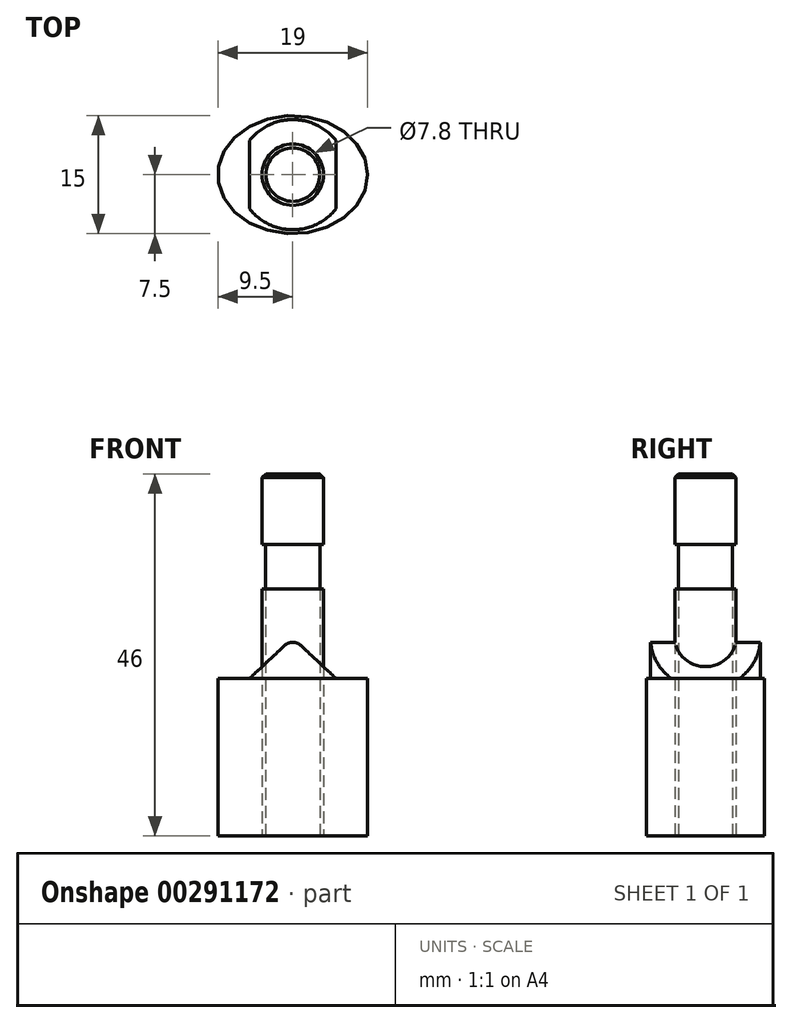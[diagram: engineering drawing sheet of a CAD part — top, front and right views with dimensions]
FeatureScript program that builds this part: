
annotation { "Feature Type Name" : "Feature", "Feature Type Description" : "" }
export const myFeature = defineFeature(function(context is Context, id is Id, definition is map)
    precondition{}
    {
        {
            var Q0;
            Q0=qCreatedBy(makeId("Top.planeOp"),FACE);
            var sketch = newSketch(context, id + "F0", { "sketchPlane" : qUnion([Q0])});
            skEllipse(sketch, "E0", {"center": v(0, 0) * mm, "majorRadius": 9.5 * mm, "minorRadius": 7.5 * mm, "majorAxis": v(1, 0)});
            skSolve(sketch);
        }
        {
            var Q0;
            Q0=makeQuery(id+"F0.imprint","IMPRINT",FACE,{"disambiguationData":[TD([[makeQuery(id+"F0.imprint","IMPRINT",EDGE,{"derivedFrom":sQuery(id+"F0.wireOp",EDGE,"E0")}),1.0]])]});
            extrude(context, id + "F1", {"entities" : qUnion([Q0]), "depth" : 20 * mm});
        }
        {
            var Q0;
            Q0=makeQuery(id+"F1.opExtrude","CAP_FACE",FACE,{"disambiguationData":[OSD([sQuery(id+"F0.wireOp",EDGE,"E0")])],"isStart":false});
            var sketch = newSketch(context, id + "F2", { "sketchPlane" : qUnion([Q0])});
            skCircle(sketch, "E1", {"center": v(0, 0) * mm, "radius": 7 * mm});
            skSolve(sketch);
        }
        {
            var Q0;
            Q0=makeQuery(id+"F2.imprint","IMPRINT",FACE,{"disambiguationData":[TD([[makeQuery(id+"F2.imprint","IMPRINT",EDGE,{"derivedFrom":sQuery(id+"F2.wireOp",EDGE,"E1")}),1.0]])]});
            extrude(context, id + "F3", {"entities" : qUnion([Q0]), "operationType" : NewBodyOperationType.ADD, "depth" : 4.6 * mm});
        }
        {
            var Q0;
            Q0=qCreatedBy(makeId("Front.planeOp"),FACE);
            var sketch = newSketch(context, id + "F4", { "sketchPlane" : qUnion([Q0])});
            skLineSegment(sketch, "E2.top", {"start": v(0, 24.6) * mm, "end": v(0, 24.6) * mm});
            skLineSegment(sketch, "E3", {"start": v(-5.5, 20) * mm, "end": v(-1.03, 24.2) * mm});
            skLineSegment(sketch, "E4", {"start": v(1.03, 24.2) * mm, "end": v(5.5, 20) * mm});
            skPoint(sketch, "E5.visualSharp", {"position": v(-0.6, 24.6) * mm});
            skArc(sketch, "E5.filletArc", {"start": v(0, 24.6) * mm, "mid": v(-0.55, 24.5) * mm, "end": v(-1.03, 24.2) * mm});
            skPoint(sketch, "E6.visualSharp", {"position": v(0.6, 24.6) * mm});
            skArc(sketch, "E6.filletArc", {"start": v(1.03, 24.2) * mm, "mid": v(0.55, 24.5) * mm, "end": v(0, 24.6) * mm});
            skLineSegment(sketch, "E7", {"start": v(-5.5, 20) * mm, "end": v(-7.13, 20) * mm});
            skLineSegment(sketch, "E8", {"start": v(-7.13, 20) * mm, "end": v(-7.13, 24.6) * mm});
            skLineSegment(sketch, "E9", {"start": v(-7.13, 24.6) * mm, "end": v(7.3, 24.6) * mm});
            skLineSegment(sketch, "E10", {"start": v(7.3, 24.6) * mm, "end": v(7.3, 20) * mm});
            skLineSegment(sketch, "E11", {"start": v(7.3, 20) * mm, "end": v(5.5, 20) * mm});
            skSolve(sketch);
        }
        {
            var Q0;
            Q0=qSketchRegion(id+"F4",true);
            extrude(context, id + "F5", {"entities" : qUnion([Q0]), "operationType" : NewBodyOperationType.REMOVE, "oppositeDirection" : true, "depth" : 25 * mm, "symmetric" : true});
        }
        {
            var Q0;
            Q0=makeQuery(id+"F1.opExtrude","CAP_FACE",FACE,{"disambiguationData":[OSD([sQuery(id+"F0.wireOp",EDGE,"E0")])],"isStart":true});
            var sketch = newSketch(context, id + "F6", { "sketchPlane" : qUnion([Q0])});
            skCircle(sketch, "E12", {"center": v(0, 0) * mm, "radius": 3.9 * mm});
            skSolve(sketch);
        }
        {
            var Q0;
            Q0=makeQuery(id+"F6.imprint","IMPRINT",FACE,{"disambiguationData":[TD([[makeQuery(id+"F6.imprint","IMPRINT",EDGE,{"derivedFrom":sQuery(id+"F6.wireOp",EDGE,"E12")}),1.0]])]});
            extrude(context, id + "F7", {"entities" : qUnion([Q0]), "operationType" : NewBodyOperationType.REMOVE, "endBound" : BoundingType.THROUGH_ALL, "oppositeDirection" : true, "depth" : 25 * mm});
        }
        {
            var Q0;
            Q0=qCreatedBy(makeId("Top.planeOp"),FACE);
            var sketch = newSketch(context, id + "F8", { "sketchPlane" : qUnion([Q0])});
            skCircle(sketch, "E13", {"center": v(0, 0) * mm, "radius": 3.45 * mm});
            skSolve(sketch);
        }
        {
            var Q0;
            Q0=qSketchRegion(id+"F8",true);
            extrude(context, id + "F9", {"entities" : qUnion([Q0]), "operationType" : NewBodyOperationType.ADD, "depth" : 46 * mm});
        }
        {
            var Q0;
            Q0=qCreatedBy(makeId("Top.planeOp"),FACE);
            var sketch = newSketch(context, id + "F10", { "sketchPlane" : qUnion([Q0])});
            skCircle(sketch, "E14", {"center": v(0, 0) * mm, "radius": 3.9 * mm});
            skSolve(sketch);
        }
        {
            var Q0;
            Q0=qSketchRegion(id+"F10",true);
            extrude(context, id + "F11", {"entities" : qUnion([Q0]), "depth" : 31.4 * mm});
        }
        {
            var Q0;
            Q0=makeQuery(id+"F9.opExtrude","CAP_FACE",FACE,{"disambiguationData":[OSD([sQuery(id+"F8.wireOp",EDGE,"E13")])],"isStart":false});
            var sketch = newSketch(context, id + "F12", { "sketchPlane" : qUnion([Q0])});
            skCircle(sketch, "E15", {"center": v(0, 0) * mm, "radius": 3.9 * mm});
            skSolve(sketch);
        }
        {
            var Q0;
            Q0=qSketchRegion(id+"F12",true);
            extrude(context, id + "F13", {"entities" : qUnion([Q0]), "operationType" : NewBodyOperationType.ADD, "oppositeDirection" : true, "depth" : 9 * mm});
        }
        {
            var Q0;
            Q0=makeQuery(id+"F13.opExtrude","CAP_EDGE",EDGE,{"disambiguationData":[OSD([sQuery(id+"F12.wireOp",EDGE,"E15")])],"isStart":true});
            chamfer(context, id + "F14", {"entities" : qUnion([Q0]), "width" : 0.5 * mm, "tangentPropagation" : true});
        }
    });
